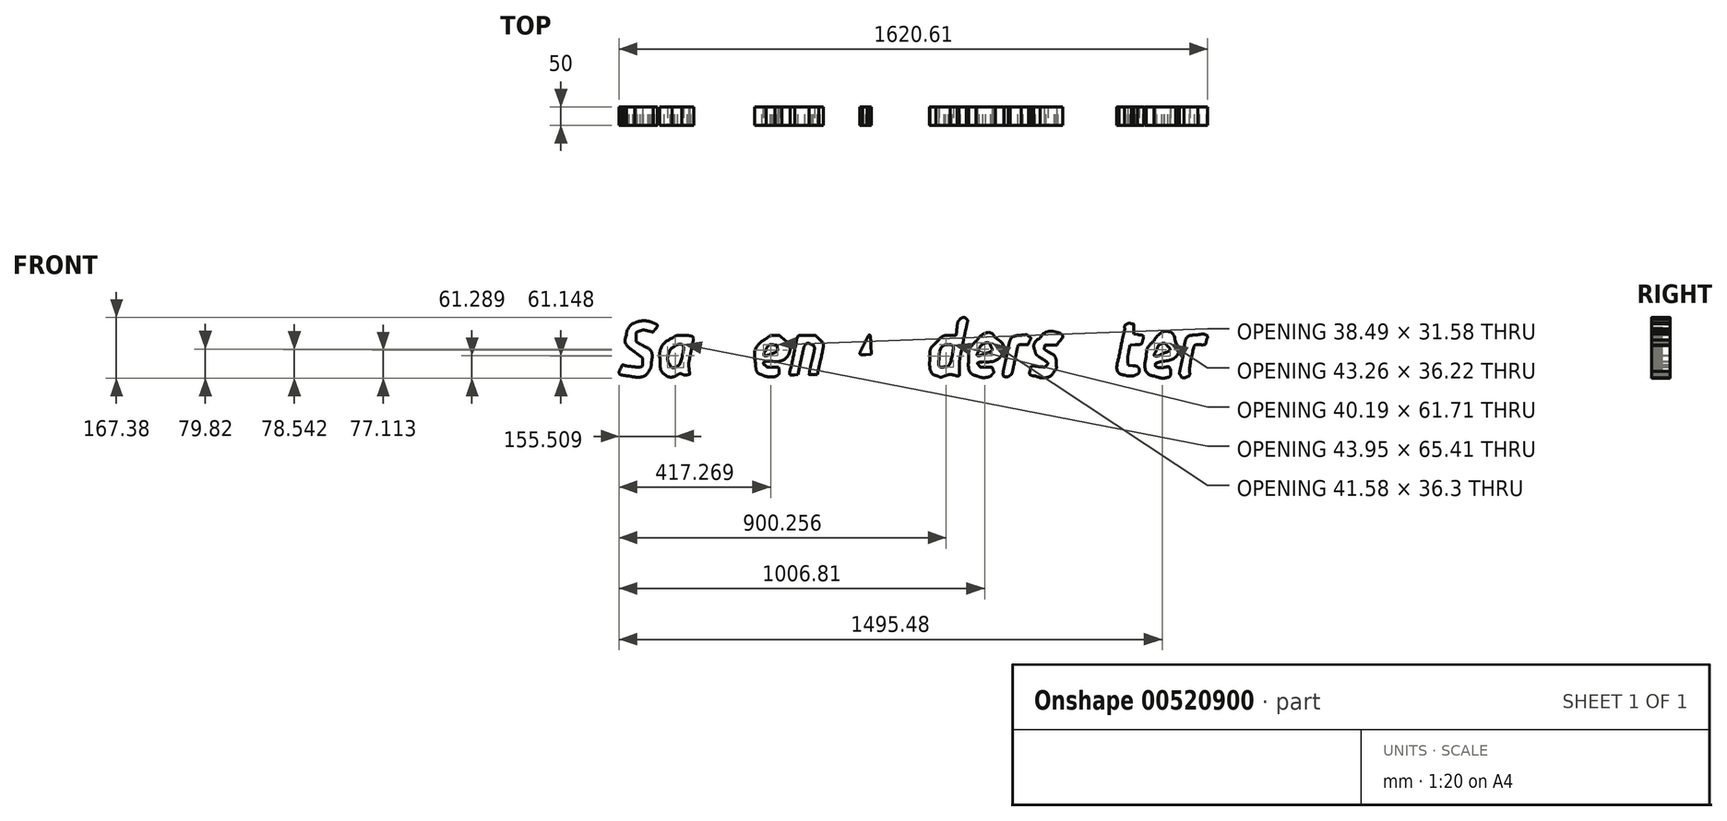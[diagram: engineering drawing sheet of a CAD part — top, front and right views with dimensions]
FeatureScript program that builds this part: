
annotation { "Feature Type Name" : "Feature", "Feature Type Description" : "" }
export const myFeature = defineFeature(function(context is Context, id is Id, definition is map)
    precondition{}
    {
        {
            var Q0;
            Q0=qCreatedBy(makeId("Front.planeOp"),FACE);
            var sketch = newSketch(context, id + "F0", { "sketchPlane" : qUnion([Q0])});
            skFitSpline(sketch, "E0", {"points": [v(-832.4, -78.37) * mm, v(-856.57, -74.84) * mm, v(-860.83, -70.17) * mm, v(-854.65, -53.92) * mm]});
            skFitSpline(sketch, "E1", {"points": [v(-854.65, -53.92) * mm, v(-852.6, -48.55) * mm, v(-851.2, -47.87) * mm, v(-845.3, -49.44) * mm]});
            skFitSpline(sketch, "E2", {"points": [v(-845.3, -49.44) * mm, v(-841.47, -50.45) * mm, v(-831.1, -51.83) * mm, v(-822.26, -52.5) * mm]});
            skFitSpline(sketch, "E3", {"points": [v(-822.26, -52.5) * mm, v(-803.08, -53.94) * mm, v(-796.37, -49.8) * mm, v(-796.37, -36.54) * mm]});
            skFitSpline(sketch, "E4", {"points": [v(-796.37, -36.54) * mm, v(-796.37, -29.53) * mm, v(-798.43, -26.67) * mm, v(-809.72, -18.05) * mm]});
            skFitSpline(sketch, "E5", {"points": [v(-809.72, -18.05) * mm, v(-836.26, 2.22) * mm, v(-844.67, 16.23) * mm, v(-841.08, 34.18) * mm]});
            skFitSpline(sketch, "E6", {"points": [v(-841.08, 34.18) * mm, v(-838.41, 47.53) * mm, v(-827.05, 63.97) * mm, v(-817.83, 67.82) * mm]});
            skFitSpline(sketch, "E7", {"points": [v(-817.83, 67.82) * mm, v(-806.68, 72.48) * mm, v(-778.28, 72.42) * mm, v(-767.03, 67.72) * mm]});
            skFitSpline(sketch, "E8", {"points": [v(-767.03, 67.72) * mm, v(-757.03, 63.54) * mm, v(-755.86, 58.07) * mm, v(-762.98, 48.8) * mm]});
            skFitSpline(sketch, "E9", {"points": [v(-762.98, 48.8) * mm, v(-767.45, 42.99) * mm, v(-768.18, 42.87) * mm, v(-780.63, 45.86) * mm]});
            skFitSpline(sketch, "E10", {"points": [v(-780.63, 45.86) * mm, v(-790.5, 48.22) * mm, v(-795.74, 48.27) * mm, v(-802.4, 46.07) * mm]});
            skFitSpline(sketch, "E11", {"points": [v(-802.4, 46.07) * mm, v(-812.07, 42.88) * mm, v(-814.18, 39.48) * mm, v(-814.18, 27.07) * mm]});
            skFitSpline(sketch, "E12", {"points": [v(-814.18, 27.07) * mm, v(-814.18, 17.85) * mm, v(-811.14, 14.56) * mm, v(-793.18, 4.3) * mm]});
            skFitSpline(sketch, "E13", {"points": [v(-793.18, 4.3) * mm, v(-776.34, -5.3) * mm, v(-769.88, -18.35) * mm, v(-771.56, -39.36) * mm]});
            skFitSpline(sketch, "E14", {"points": [v(-771.56, -39.36) * mm, v(-772.26, -48.1) * mm, v(-774.81, -58.03) * mm, v(-777.34, -61.88) * mm]});
            skFitSpline(sketch, "E15", {"points": [v(-777.34, -61.88) * mm, v(-786.08, -75.22) * mm, v(-808.33, -81.88) * mm, v(-832.4, -78.37) * mm]});
            skFitSpline(sketch, "E16", {"points": [v(13.27, -77.43) * mm, v(1.65, -72.38) * mm, v(-5.13, -55.86) * mm, v(-5.13, -32.6) * mm]});
            skFitSpline(sketch, "E17", {"points": [v(-5.13, -32.6) * mm, v(-5.13, -11.48) * mm, v(-0.66, 0.47) * mm, v(12.17, 13.69) * mm]});
            skFitSpline(sketch, "E18", {"points": [v(12.17, 13.69) * mm, v(26.49, 28.44) * mm, v(36.2, 33.5) * mm, v(50.88, 33.83) * mm]});
            skFitSpline(sketch, "E19", {"points": [v(50.88, 33.83) * mm, v(65.98, 34.17) * mm, v(67.23, 35.7) * mm, v(69.79, 56.78) * mm]});
            skFitSpline(sketch, "E20", {"points": [v(69.79, 56.78) * mm, v(70.76, 64.83) * mm, v(73.28, 73.13) * mm, v(75.37, 75.22) * mm]});
            skFitSpline(sketch, "E21", {"points": [v(75.37, 75.22) * mm, v(81.33, 81.18) * mm, v(91.43, 82.8) * mm, v(95.74, 78.49) * mm]});
            skFitSpline(sketch, "E22", {"points": [v(95.74, 78.49) * mm, v(99.06, 75.17) * mm, v(99.03, 72.66) * mm, v(95.5, 57.17) * mm]});
            skFitSpline(sketch, "E23", {"points": [v(95.5, 57.17) * mm, v(93.29, 47.5) * mm, v(89.09, 27.59) * mm, v(86.16, 12.9) * mm]});
            skFitSpline(sketch, "E24", {"points": [v(86.16, 12.9) * mm, v(83.24, -1.8) * mm, v(79.87, -18.4) * mm, v(78.67, -24) * mm]});
            skFitSpline(sketch, "E25", {"points": [v(78.67, -24) * mm, v(77.48, -29.6) * mm, v(76.46, -42.97) * mm, v(76.4, -53.72) * mm]});
            skFitSpline(sketch, "E26", {"points": [v(76.4, -53.72) * mm, v(76.27, -75.6) * mm, v(73.96, -78.2) * mm, v(57.4, -75.09) * mm]});
            skFitSpline(sketch, "E27", {"points": [v(57.4, -75.09) * mm, v(52.56, -74.18) * mm, v(44.62, -75.13) * mm, v(38.22, -77.39) * mm]});
            skFitSpline(sketch, "E28", {"points": [v(38.22, -77.39) * mm, v(25.08, -82.03) * mm, v(23.86, -82.03) * mm, v(13.27, -77.43) * mm]});
            skFitSpline(sketch, "E29", {"points": [v(45.61, -49.61) * mm, v(50.04, -44.27) * mm, v(59.23, 2.98) * mm, v(56.38, 5.82) * mm]});
            skFitSpline(sketch, "E30", {"points": [v(56.38, 5.82) * mm, v(55.1, 7.12) * mm, v(50.28, 7.8) * mm, v(45.7, 7.35) * mm]});
            skFitSpline(sketch, "E31", {"points": [v(45.7, 7.35) * mm, v(32.67, 6.07) * mm, v(22.2, -8.6) * mm, v(20.83, -27.5) * mm]});
            skFitSpline(sketch, "E32", {"points": [v(20.83, -27.5) * mm, v(19.44, -46.7) * mm, v(22.82, -53.26) * mm, v(34.08, -53.26) * mm]});
            skFitSpline(sketch, "E33", {"points": [v(34.08, -53.26) * mm, v(38.76, -53.26) * mm, v(43.95, -51.62) * mm, v(45.61, -49.61) * mm]});
            skFitSpline(sketch, "E34", {"points": [v(125.9, -78.32) * mm, v(108.94, -72.06) * mm, v(101.73, -58.36) * mm, v(101.73, -32.42) * mm]});
            skFitSpline(sketch, "E35", {"points": [v(101.73, -32.42) * mm, v(101.73, -12.23) * mm, v(107.6, 2.14) * mm, v(121.97, 17.13) * mm]});
            skFitSpline(sketch, "E36", {"points": [v(121.97, 17.13) * mm, v(140.93, 36.9) * mm, v(162.21, 41.06) * mm, v(174.93, 27.48) * mm]});
            skFitSpline(sketch, "E37", {"points": [v(174.93, 27.48) * mm, v(198.93, 1.86) * mm, v(180.94, -33.1) * mm, v(140.47, -39.49) * mm]});
            skFitSpline(sketch, "E38", {"points": [v(140.47, -39.49) * mm, v(127.69, -41.5) * mm, v(126.1, -43.2) * mm, v(130.86, -49.7) * mm]});
            skFitSpline(sketch, "E39", {"points": [v(130.86, -49.7) * mm, v(133.68, -53.56) * mm, v(137.62, -54.53) * mm, v(150.43, -54.53) * mm]});
            skFitSpline(sketch, "E40", {"points": [v(150.43, -54.53) * mm, v(165.66, -54.53) * mm, v(166.59, -54.88) * mm, v(168.95, -61.58) * mm]});
            skFitSpline(sketch, "E41", {"points": [v(168.95, -61.58) * mm, v(171, -67.37) * mm, v(170.51, -69.56) * mm, v(166.27, -73.8) * mm]});
            skFitSpline(sketch, "E42", {"points": [v(166.27, -73.8) * mm, v(160.04, -80.03) * mm, v(137.38, -82.56) * mm, v(125.9, -78.32) * mm]});
            skFitSpline(sketch, "E43", {"points": [v(148.39, -16.11) * mm, v(162.02, -11.46) * mm, v(166.94, -5.04) * mm, v(162.79, 2.72) * mm]});
            skFitSpline(sketch, "E44", {"points": [v(162.79, 2.72) * mm, v(157.07, 13.4) * mm, v(135.12, 5.48) * mm, v(129.5, -9.28) * mm]});
            skFitSpline(sketch, "E45", {"points": [v(129.5, -9.28) * mm, v(125.08, -20.9) * mm, v(129.56, -22.52) * mm, v(148.39, -16.11) * mm]});
            skFitSpline(sketch, "E46", {"points": [v(285.26, -78.7) * mm, v(272.13, -75.6) * mm, v(269.24, -71.47) * mm, v(272.34, -60.25) * mm]});
            skFitSpline(sketch, "E47", {"points": [v(293.34, -52.35) * mm, v(307.97, -53.59) * mm, v(312.38, -53.12) * mm, v(314.9, -50.09) * mm]});
            skFitSpline(sketch, "E48", {"points": [v(314.9, -50.09) * mm, v(319.65, -44.36) * mm, v(316.58, -39.62) * mm, v(301.31, -29.1) * mm]});
            skFitSpline(sketch, "E49", {"points": [v(301.31, -29.1) * mm, v(290.26, -21.5) * mm, v(286.93, -17.53) * mm, v(284.72, -9.33) * mm]});
            skFitSpline(sketch, "E50", {"points": [v(284.72, -9.33) * mm, v(281.07, 4.25) * mm, v(285.57, 16.14) * mm, v(298.24, 26.4) * mm]});
            skFitSpline(sketch, "E51", {"points": [v(298.24, 26.4) * mm, v(320.16, 44.13) * mm, v(359.88, 33.93) * mm, v(348.4, 13.5) * mm]});
            skFitSpline(sketch, "E52", {"points": [v(348.4, 13.5) * mm, v(344.77, 7.03) * mm, v(343.32, 6.53) * mm, v(328.05, 6.53) * mm]});
            skFitSpline(sketch, "E53", {"points": [v(328.05, 6.53) * mm, v(313.06, 6.53) * mm, v(311.55, 6.04) * mm, v(310.82, 0.94) * mm]});
            skFitSpline(sketch, "E54", {"points": [v(310.82, 0.94) * mm, v(310.24, -3.2) * mm, v(312.55, -6.26) * mm, v(319.73, -10.84) * mm]});
            skFitSpline(sketch, "E55", {"points": [v(319.73, -10.84) * mm, v(336.4, -21.47) * mm, v(341.61, -28.9) * mm, v(342.82, -43.7) * mm]});
            skFitSpline(sketch, "E56", {"points": [v(342.82, -43.7) * mm, v(343.73, -54.78) * mm, v(342.93, -58.33) * mm, v(338.15, -64.39) * mm]});
            skFitSpline(sketch, "E57", {"points": [v(338.15, -64.39) * mm, v(327.14, -78.34) * mm, v(306.9, -83.81) * mm, v(285.26, -78.7) * mm]});
            skLineSegment(sketch, "E58", {"start": v(272.34, -60.25) * mm, "end": v(274.95, -50.8) * mm});
            skLineSegment(sketch, "E59", {"start": v(274.95, -50.8) * mm, "end": v(293.34, -52.35) * mm});
            skFitSpline(sketch, "E60", {"points": [v(416.9, -77.4) * mm, v(400.2, -72.07) * mm, v(397.47, -68.03) * mm, v(402.89, -56.67) * mm]});
            skFitSpline(sketch, "E61", {"points": [v(402.89, -56.67) * mm, v(406.73, -48.61) * mm, v(407.97, -47.81) * mm, v(414.11, -49.45) * mm]});
            skFitSpline(sketch, "E62", {"points": [v(414.11, -49.45) * mm, v(417.91, -50.46) * mm, v(428.02, -51.82) * mm, v(436.58, -52.47) * mm]});
            skFitSpline(sketch, "E63", {"points": [v(436.58, -52.47) * mm, v(451.13, -53.58) * mm, v(452.48, -53.21) * mm, v(457.57, -46.75) * mm]});
            skFitSpline(sketch, "E64", {"points": [v(457.57, -46.75) * mm, v(466.75, -35.08) * mm, v(466.96, -35.45) * mm, v(431.27, -2.8) * mm]});
            skFitSpline(sketch, "E65", {"points": [v(431.27, -2.8) * mm, v(415.1, 12) * mm, v(412.84, 28.92) * mm, v(424.26, 49.67) * mm]});
            skFitSpline(sketch, "E66", {"points": [v(424.26, 49.67) * mm, v(433.77, 66.95) * mm, v(443.58, 72.21) * mm, v(466.48, 72.32) * mm]});
            skFitSpline(sketch, "E67", {"points": [v(466.48, 72.32) * mm, v(495, 72.44) * mm, v(506.72, 63.65) * mm, v(498.5, 48.3) * mm]});
            skFitSpline(sketch, "E68", {"points": [v(498.5, 48.3) * mm, v(496.08, 43.78) * mm, v(494.02, 43.47) * mm, v(475.94, 44.98) * mm]});
            skFitSpline(sketch, "E69", {"points": [v(475.94, 44.98) * mm, v(457.8, 46.5) * mm, v(455.56, 46.16) * mm, v(450.61, 41.22) * mm]});
            skFitSpline(sketch, "E70", {"points": [v(450.61, 41.22) * mm, v(438.92, 29.53) * mm, v(444.77, 18.04) * mm, v(470.63, 1.88) * mm]});
            skFitSpline(sketch, "E71", {"points": [v(470.63, 1.88) * mm, v(480.9, -4.54) * mm, v(490.98, -22.57) * mm, v(490.98, -34.5) * mm]});
            skFitSpline(sketch, "E72", {"points": [v(490.98, -34.5) * mm, v(490.98, -44.42) * mm, v(483.22, -63.14) * mm, v(476.68, -68.98) * mm]});
            skFitSpline(sketch, "E73", {"points": [v(476.68, -68.98) * mm, v(465.2, -79.23) * mm, v(435.67, -83.4) * mm, v(416.9, -77.4) * mm]});
            skFitSpline(sketch, "E74", {"points": [v(614.68, -78.6) * mm, v(596.44, -73.15) * mm, v(587.03, -53.04) * mm, v(590.24, -26.35) * mm]});
            skFitSpline(sketch, "E75", {"points": [v(590.24, -26.35) * mm, v(592.6, -6.7) * mm, v(597.58, 3.7) * mm, v(611.7, 18.43) * mm]});
            skFitSpline(sketch, "E76", {"points": [v(611.7, 18.43) * mm, v(634.54, 42.27) * mm, v(661.63, 40.55) * mm, v(671.45, 14.64) * mm]});
            skFitSpline(sketch, "E77", {"points": [v(671.45, 14.64) * mm, v(680.86, -10.2) * mm, v(666.7, -29.94) * mm, v(633.46, -38.3) * mm]});
            skFitSpline(sketch, "E78", {"points": [v(633.46, -38.3) * mm, v(623.4, -40.84) * mm, v(616.92, -43.81) * mm, v(616.92, -45.88) * mm]});
            skFitSpline(sketch, "E79", {"points": [v(616.92, -45.88) * mm, v(616.92, -51.83) * mm, v(628.77, -55.84) * mm, v(641.48, -54.2) * mm]});
            skFitSpline(sketch, "E80", {"points": [v(641.48, -54.2) * mm, v(651.92, -52.85) * mm, v(653.67, -53.33) * mm, v(656.32, -58.29) * mm]});
            skFitSpline(sketch, "E81", {"points": [v(656.32, -58.29) * mm, v(657.98, -61.38) * mm, v(658.65, -66.61) * mm, v(657.82, -69.92) * mm]});
            skFitSpline(sketch, "E82", {"points": [v(657.82, -69.92) * mm, v(655.43, -79.46) * mm, v(632.77, -84.03) * mm, v(614.68, -78.6) * mm]});
            skFitSpline(sketch, "E83", {"points": [v(639.66, -15.16) * mm, v(653.29, -9.32) * mm, v(656.23, -4.17) * mm, v(649.9, 2.81) * mm]});
            skFitSpline(sketch, "E84", {"points": [v(649.9, 2.81) * mm, v(641.53, 12.07) * mm, v(626.43, 7.35) * mm, v(619.78, -6.61) * mm]});
            skFitSpline(sketch, "E85", {"points": [v(619.78, -6.61) * mm, v(612.8, -21.25) * mm, v(619.11, -23.97) * mm, v(639.66, -15.16) * mm]});
            skFitSpline(sketch, "E86", {"points": [v(-735.87, -72.96) * mm, v(-743.4, -66.75) * mm, v(-747.86, -52.1) * mm, v(-747.96, -33.2) * mm]});
            skFitSpline(sketch, "E87", {"points": [v(-747.96, -33.2) * mm, v(-748.1, -8.56) * mm, v(-736.42, 12.55) * mm, v(-715.2, 26) * mm]});
            skFitSpline(sketch, "E88", {"points": [v(-715.2, 26) * mm, v(-705.73, 32) * mm, v(-701.01, 33.25) * mm, v(-687.61, 33.25) * mm]});
            skFitSpline(sketch, "E89", {"points": [v(-687.61, 33.25) * mm, v(-671.7, 33.25) * mm, v(-656.44, 28.2) * mm, v(-656.44, 22.93) * mm]});
            skFitSpline(sketch, "E90", {"points": [v(-656.44, 22.93) * mm, v(-656.44, 21.53) * mm, v(-659.4, 5.82) * mm, v(-663.02, -11.99) * mm]});
            skFitSpline(sketch, "E91", {"points": [v(-663.02, -11.99) * mm, v(-667.89, -35.9) * mm, v(-669.19, -48.15) * mm, v(-668, -58.9) * mm]});
            skFitSpline(sketch, "E92", {"points": [v(-668, -58.9) * mm, v(-666.42, -73.04) * mm, v(-666.57, -73.5) * mm, v(-673.04, -75.13) * mm]});
            skFitSpline(sketch, "E93", {"points": [v(-673.04, -75.13) * mm, v(-676.71, -76.05) * mm, v(-682.54, -75.5) * mm, v(-686, -73.93) * mm]});
            skFitSpline(sketch, "E94", {"points": [v(-686, -73.93) * mm, v(-690.95, -71.68) * mm, v(-693.9, -71.88) * mm, v(-699.68, -74.88) * mm]});
            skFitSpline(sketch, "E95", {"points": [v(-699.68, -74.88) * mm, v(-710.86, -80.66) * mm, v(-727.61, -79.77) * mm, v(-735.87, -72.96) * mm]});
            skFitSpline(sketch, "E96", {"points": [v(-699.02, -50.08) * mm, v(-694.76, -46.83) * mm, v(-683.42, 1.57) * mm, v(-685.96, 5.69) * mm]});
            skFitSpline(sketch, "E97", {"points": [v(-685.96, 5.69) * mm, v(-688.13, 9.2) * mm, v(-700.72, 8.07) * mm, v(-706.79, 3.82) * mm]});
            skFitSpline(sketch, "E98", {"points": [v(-706.79, 3.82) * mm, v(-719.65, -5.19) * mm, v(-727.15, -34.9) * mm, v(-719.95, -48.33) * mm]});
            skFitSpline(sketch, "E99", {"points": [v(-719.95, -48.33) * mm, v(-716.92, -54) * mm, v(-705.45, -54.96) * mm, v(-699.02, -50.08) * mm]});
            skFitSpline(sketch, "E100", {"points": [v(-467.34, -74.99) * mm, v(-478.7, -70.04) * mm, v(-483.32, -61.6) * mm, v(-485.1, -42.54) * mm]});
            skFitSpline(sketch, "E101", {"points": [v(-485.1, -42.54) * mm, v(-487.7, -14.63) * mm, v(-478.08, 7.64) * mm, v(-456.16, 24.38) * mm]});
            skFitSpline(sketch, "E102", {"points": [v(-456.16, 24.38) * mm, v(-446.34, 31.87) * mm, v(-442.5, 33.25) * mm, v(-431.36, 33.25) * mm]});
            skFitSpline(sketch, "E103", {"points": [v(-431.36, 33.25) * mm, v(-420.87, 33.25) * mm, v(-417.14, 32.07) * mm, v(-413.13, 27.52) * mm]});
            skFitSpline(sketch, "E104", {"points": [v(-413.13, 27.52) * mm, v(-389.9, 1.19) * mm, v(-406.36, -33.37) * mm, v(-443.95, -37.25) * mm]});
            skFitSpline(sketch, "E105", {"points": [v(-443.95, -37.25) * mm, v(-459.68, -38.88) * mm, v(-464.06, -43.19) * mm, v(-457.09, -50.16) * mm]});
            skFitSpline(sketch, "E106", {"points": [v(-457.09, -50.16) * mm, v(-454.17, -53.08) * mm, v(-448.23, -54.34) * mm, v(-437.02, -54.42) * mm]});
            skFitSpline(sketch, "E107", {"points": [v(-420.26, -63.32) * mm, v(-419.68, -69.5) * mm, v(-420.77, -73.1) * mm, v(-423.93, -75.4) * mm]});
            skFitSpline(sketch, "E108", {"points": [v(-423.93, -75.4) * mm, v(-429.86, -79.74) * mm, v(-457.02, -79.47) * mm, v(-467.34, -74.99) * mm]});
            skLineSegment(sketch, "E109", {"start": v(-437.02, -54.42) * mm, "end": v(-421.1, -54.53) * mm});
            skLineSegment(sketch, "E110", {"start": v(-421.1, -54.53) * mm, "end": v(-420.26, -63.32) * mm});
            skFitSpline(sketch, "E111", {"points": [v(-442.47, -17.28) * mm, v(-430.03, -13.1) * mm, v(-424.55, -7.53) * mm, v(-425.43, 0.04) * mm]});
            skFitSpline(sketch, "E112", {"points": [v(-425.43, 0.04) * mm, v(-426.02, 5.1) * mm, v(-427.82, 6.72) * mm, v(-433.6, 7.38) * mm]});
            skFitSpline(sketch, "E113", {"points": [v(-433.6, 7.38) * mm, v(-443.8, 8.54) * mm, v(-451.41, 3.87) * mm, v(-456.4, -6.6) * mm]});
            skFitSpline(sketch, "E114", {"points": [v(-456.4, -6.6) * mm, v(-462.82, -20.05) * mm, v(-459.13, -22.87) * mm, v(-442.47, -17.28) * mm]});
            skFitSpline(sketch, "E115", {"points": [v(-249.22, -76.3) * mm, v(-252.22, -74.4) * mm, v(-248.62, -65.43) * mm, v(-229.57, -27.36) * mm]});
            skFitSpline(sketch, "E116", {"points": [v(-229.57, -27.36) * mm, v(-205.24, 21.28) * mm, v(-184.06, 59.36) * mm, v(-177.11, 66.96) * mm]});
            skFitSpline(sketch, "E117", {"points": [v(-177.11, 66.96) * mm, v(-172.39, 72.13) * mm, v(-157.07, 72.95) * mm, v(-153.37, 68.23) * mm]});
            skFitSpline(sketch, "E118", {"points": [v(-153.37, 68.23) * mm, v(-150.18, 64.16) * mm, v(-146.46, 39.3) * mm, v(-139.84, -22.27) * mm]});
            skFitSpline(sketch, "E119", {"points": [v(-139.84, -22.27) * mm, v(-134.1, -75.62) * mm, v(-134.51, -78.73) * mm, v(-147.28, -78.66) * mm]});
            skFitSpline(sketch, "E120", {"points": [v(-147.28, -78.66) * mm, v(-158.15, -78.6) * mm, v(-161.33, -74.85) * mm, v(-162.78, -60.4) * mm]});
            skFitSpline(sketch, "E121", {"points": [v(-188.96, -46.17) * mm, v(-216.5, -45.36) * mm, v(-213.34, -43.52) * mm, v(-221.32, -65.01) * mm]});
            skFitSpline(sketch, "E122", {"points": [v(-221.32, -65.01) * mm, v(-225.5, -76.26) * mm, v(-240.01, -82.13) * mm, v(-249.22, -76.3) * mm]});
            skLineSegment(sketch, "E123", {"start": v(-162.78, -60.4) * mm, "end": v(-164.14, -46.9) * mm});
            skLineSegment(sketch, "E124", {"start": v(-164.14, -46.9) * mm, "end": v(-188.96, -46.17) * mm});
            skFitSpline(sketch, "E125", {"points": [v(-167.57, 6.53) * mm, v(-168.06, 20.53) * mm, v(-169.4, 32.97) * mm, v(-170.54, 34.19) * mm]});
            skFitSpline(sketch, "E126", {"points": [v(-170.54, 34.19) * mm, v(-171.7, 35.4) * mm, v(-174.85, 31.97) * mm, v(-177.56, 26.55) * mm]});
            skFitSpline(sketch, "E127", {"points": [v(-177.56, 26.55) * mm, v(-180.28, 21.14) * mm, v(-186.14, 9.52) * mm, v(-190.6, 0.74) * mm]});
            skFitSpline(sketch, "E128", {"points": [v(-190.6, 0.74) * mm, v(-195.05, -8.05) * mm, v(-197.98, -16.4) * mm, v(-197.1, -17.83) * mm]});
            skFitSpline(sketch, "E129", {"points": [v(-197.1, -17.83) * mm, v(-196.21, -19.26) * mm, v(-189.01, -20.08) * mm, v(-181.09, -19.67) * mm]});
            skFitSpline(sketch, "E130", {"points": [v(-113.55, -75.03) * mm, v(-115.05, -71.12) * mm, v(-104.47, -16.2) * mm, v(-97.4, 8.79) * mm]});
            skFitSpline(sketch, "E131", {"points": [v(-97.4, 8.79) * mm, v(-92.42, 26.38) * mm, v(-85.25, 32.09) * mm, v(-64.93, 34.63) * mm]});
            skFitSpline(sketch, "E132", {"points": [v(-64.93, 34.63) * mm, v(-39.6, 37.8) * mm, v(-22.92, 22.87) * mm, v(-22.95, -2.9) * mm]});
            skFitSpline(sketch, "E133", {"points": [v(-22.95, -2.9) * mm, v(-22.97, -16.06) * mm, v(-34.26, -70.68) * mm, v(-37.66, -74.08) * mm]});
            skFitSpline(sketch, "E134", {"points": [v(-37.66, -74.08) * mm, v(-38.99, -75.41) * mm, v(-44.52, -76.14) * mm, v(-49.95, -75.7) * mm]});
            skFitSpline(sketch, "E135", {"points": [v(-49.95, -75.7) * mm, v(-61.62, -74.73) * mm, v(-61.42, -77.03) * mm, v(-53.6, -33.73) * mm]});
            skFitSpline(sketch, "E136", {"points": [v(-53.6, -33.73) * mm, v(-46.92, 3.18) * mm, v(-48.16, 8.57) * mm, v(-63, 7.31) * mm]});
            skLineSegment(sketch, "E137", {"start": v(-181.09, -19.67) * mm, "end": v(-166.68, -18.9) * mm});
            skLineSegment(sketch, "E138", {"start": v(-166.68, -18.9) * mm, "end": v(-167.57, 6.53) * mm});
            skFitSpline(sketch, "E139", {"points": [v(-78.09, -18.9) * mm, v(-81.33, -32.9) * mm, v(-85.12, -50.65) * mm, v(-86.5, -58.34) * mm]});
            skFitSpline(sketch, "E140", {"points": [v(-86.5, -58.34) * mm, v(-87.91, -66.18) * mm, v(-90.93, -73.74) * mm, v(-93.36, -75.52) * mm]});
            skFitSpline(sketch, "E141", {"points": [v(-93.36, -75.52) * mm, v(-99.25, -79.84) * mm, v(-111.82, -79.54) * mm, v(-113.55, -75.03) * mm]});
            skLineSegment(sketch, "E142", {"start": v(-63, 7.31) * mm, "end": v(-72.18, 6.53) * mm});
            skLineSegment(sketch, "E143", {"start": v(-72.18, 6.53) * mm, "end": v(-78.09, -18.9) * mm});
            skFitSpline(sketch, "E144", {"points": [v(196.95, -75.31) * mm, v(196.23, -73.45) * mm, v(198.65, -57.7) * mm, v(202.32, -40.33) * mm]});
            skFitSpline(sketch, "E145", {"points": [v(202.32, -40.33) * mm, v(205.99, -22.95) * mm, v(210.14, -3.03) * mm, v(211.55, 3.93) * mm]});
            skFitSpline(sketch, "E146", {"points": [v(211.55, 3.93) * mm, v(212.96, 10.9) * mm, v(215.19, 18.61) * mm, v(216.5, 21.08) * mm]});
            skFitSpline(sketch, "E147", {"points": [v(216.5, 21.08) * mm, v(220.05, 27.7) * mm, v(230.9, 32.33) * mm, v(247.1, 34.16) * mm]});
            skFitSpline(sketch, "E148", {"points": [v(247.1, 34.16) * mm, v(258.99, 35.5) * mm, v(262.5, 34.94) * mm, v(267.42, 30.95) * mm]});
            skFitSpline(sketch, "E149", {"points": [v(267.42, 30.95) * mm, v(273.28, 26.2) * mm, v(273.3, 25.99) * mm, v(269, 16.97) * mm]});
            skFitSpline(sketch, "E150", {"points": [v(269, 16.97) * mm, v(264.84, 8.23) * mm, v(264.03, 7.8) * mm, v(251.8, 7.8) * mm]});
            skFitSpline(sketch, "E151", {"points": [v(251.8, 7.8) * mm, v(243.86, 7.8) * mm, v(238.49, 6.59) * mm, v(237.73, 4.62) * mm]});
            skFitSpline(sketch, "E152", {"points": [v(237.73, 4.62) * mm, v(237.07, 2.87) * mm, v(233.1, -15.16) * mm, v(228.94, -35.45) * mm]});
            skFitSpline(sketch, "E153", {"points": [v(228.94, -35.45) * mm, v(223.76, -60.66) * mm, v(219.99, -73.34) * mm, v(217.03, -75.52) * mm]});
            skFitSpline(sketch, "E154", {"points": [v(217.03, -75.52) * mm, v(211.3, -79.72) * mm, v(198.59, -79.59) * mm, v(196.95, -75.31) * mm]});
            skFitSpline(sketch, "E155", {"points": [v(532.76, -76.02) * mm, v(515.39, -70.85) * mm, v(509.91, -55.44) * mm, v(515.39, -27.1) * mm]});
            skFitSpline(sketch, "E156", {"points": [v(515.39, -27.1) * mm, v(524.65, 20.8) * mm, v(527.09, 32.54) * mm, v(529.3, 39.79) * mm]});
            skFitSpline(sketch, "E157", {"points": [v(529.3, 39.79) * mm, v(530.62, 44.08) * mm, v(531.7, 50.07) * mm, v(531.7, 53.09) * mm]});
            skFitSpline(sketch, "E158", {"points": [v(531.7, 53.09) * mm, v(531.7, 59.8) * mm, v(542, 67.01) * mm, v(549.99, 65.88) * mm]});
            skFitSpline(sketch, "E159", {"points": [v(549.99, 65.88) * mm, v(555.3, 65.13) * mm, v(555.86, 63.73) * mm, v(555.86, 51.06) * mm]});
            skFitSpline(sketch, "E160", {"points": [v(566.72, 35.61) * mm, v(579.84, 33.86) * mm, v(583.73, 30.47) * mm, v(581.65, 22.62) * mm]});
            skFitSpline(sketch, "E161", {"points": [v(581.65, 22.62) * mm, v(578.66, 11.4) * mm, v(575.51, 9.19) * mm, v(560.57, 7.84) * mm]});
            skLineSegment(sketch, "E162", {"start": v(555.86, 51.06) * mm, "end": v(555.86, 37.07) * mm});
            skLineSegment(sketch, "E163", {"start": v(555.86, 37.07) * mm, "end": v(566.72, 35.61) * mm});
            skFitSpline(sketch, "E164", {"points": [v(542.6, -11.28) * mm, v(540.76, -21.07) * mm, v(539.55, -33.67) * mm, v(539.92, -39.26) * mm]});
            skLineSegment(sketch, "E165", {"start": v(560.57, 7.84) * mm, "end": v(545.96, 6.53) * mm});
            skLineSegment(sketch, "E166", {"start": v(545.96, 6.53) * mm, "end": v(542.6, -11.28) * mm});
            skFitSpline(sketch, "E167", {"points": [v(553.27, -50.24) * mm, v(560.24, -50.68) * mm, v(566.8, -52.4) * mm, v(567.86, -54.06) * mm]});
            skFitSpline(sketch, "E168", {"points": [v(567.86, -54.06) * mm, v(571.4, -59.63) * mm, v(569.97, -70.83) * mm, v(565.4, -73.22) * mm]});
            skFitSpline(sketch, "E169", {"points": [v(565.4, -73.22) * mm, v(558.1, -77.06) * mm, v(541.14, -78.51) * mm, v(532.76, -76.02) * mm]});
            skLineSegment(sketch, "E170", {"start": v(539.92, -39.26) * mm, "end": v(540.6, -49.44) * mm});
            skLineSegment(sketch, "E171", {"start": v(540.6, -49.44) * mm, "end": v(553.27, -50.24) * mm});
            skFitSpline(sketch, "E172", {"points": [v(684.64, -75.24) * mm, v(682.48, -72.63) * mm, v(683.1, -65.55) * mm, v(687.16, -46.62) * mm]});
            skFitSpline(sketch, "E173", {"points": [v(687.16, -46.62) * mm, v(690.13, -32.78) * mm, v(693.45, -15.73) * mm, v(694.54, -8.73) * mm]});
            skFitSpline(sketch, "E174", {"points": [v(694.54, -8.73) * mm, v(699.21, 21.33) * mm, v(708.61, 32.14) * mm, v(732.55, 34.98) * mm]});
            skFitSpline(sketch, "E175", {"points": [v(732.55, 34.98) * mm, v(749.35, 36.97) * mm, v(759.43, 31.16) * mm, v(756.87, 20.97) * mm]});
            skFitSpline(sketch, "E176", {"points": [v(756.87, 20.97) * mm, v(754.16, 10.19) * mm, v(750.68, 7.8) * mm, v(737.6, 7.8) * mm]});
            skFitSpline(sketch, "E177", {"points": [v(737.6, 7.8) * mm, v(730.86, 7.8) * mm, v(724.75, 6.83) * mm, v(724, 5.64) * mm]});
            skFitSpline(sketch, "E178", {"points": [v(724, 5.64) * mm, v(722.28, 2.84) * mm, v(709.78, -59.9) * mm, v(709.78, -65.79) * mm]});
            skFitSpline(sketch, "E179", {"points": [v(709.78, -65.79) * mm, v(709.78, -76.17) * mm, v(691.2, -83.15) * mm, v(684.64, -75.24) * mm]});
            skFitSpline(sketch, "E180", {"points": [v(762.39, -75.9) * mm, v(757.57, -73.04) * mm, v(757.77, -65.56) * mm, v(763.27, -43.08) * mm]});
            skFitSpline(sketch, "E181", {"points": [v(763.27, -43.08) * mm, v(764.47, -38.18) * mm, v(766.6, -29.02) * mm, v(768, -22.73) * mm]});
            skFitSpline(sketch, "E182", {"points": [v(768, -22.73) * mm, v(769.4, -16.43) * mm, v(772.26, -3.84) * mm, v(774.36, 5.26) * mm]});
            skFitSpline(sketch, "E183", {"points": [v(774.36, 5.26) * mm, v(776.45, 14.36) * mm, v(780.11, 32.67) * mm, v(782.48, 45.97) * mm]});
            skFitSpline(sketch, "E184", {"points": [v(782.48, 45.97) * mm, v(787.97, 76.73) * mm, v(787.5, 75.72) * mm, v(798.04, 79.2) * mm]});
            skFitSpline(sketch, "E185", {"points": [v(798.04, 79.2) * mm, v(805.21, 81.57) * mm, v(807.66, 81.47) * mm, v(810.38, 78.69) * mm]});
            skFitSpline(sketch, "E186", {"points": [v(810.38, 78.69) * mm, v(813.23, 75.8) * mm, v(812.94, 71.24) * mm, v(808.63, 51.06) * mm]});
            skFitSpline(sketch, "E187", {"points": [v(808.63, 51.06) * mm, v(800.83, 14.47) * mm, v(798.49, -0.34) * mm, v(800.22, -2.07) * mm]});
            skFitSpline(sketch, "E188", {"points": [v(800.22, -2.07) * mm, v(801.09, -2.93) * mm, v(810.24, 5.23) * mm, v(820.57, 16.08) * mm]});
            skFitSpline(sketch, "E189", {"points": [v(820.57, 16.08) * mm, v(838.6, 35) * mm, v(843.82, 37.9) * mm, v(853.32, 34.25) * mm]});
            skFitSpline(sketch, "E190", {"points": [v(853.32, 34.25) * mm, v(861.23, 31.21) * mm, v(857.17, 22.34) * mm, v(839.53, 4.16) * mm]});
            skFitSpline(sketch, "E191", {"points": [v(839.53, 4.16) * mm, v(829.33, -6.36) * mm, v(821.73, -16.42) * mm, v(821.73, -19.39) * mm]});
            skFitSpline(sketch, "E192", {"points": [v(821.73, -19.39) * mm, v(821.73, -22.23) * mm, v(826.3, -34.34) * mm, v(831.9, -46.28) * mm]});
            skFitSpline(sketch, "E193", {"points": [v(831.9, -46.28) * mm, v(837.5, -58.23) * mm, v(842.08, -69.22) * mm, v(842.08, -70.71) * mm]});
            skFitSpline(sketch, "E194", {"points": [v(842.08, -70.71) * mm, v(842.08, -74.25) * mm, v(833.67, -78.7) * mm, v(826.98, -78.7) * mm]});
            skFitSpline(sketch, "E195", {"points": [v(826.98, -78.7) * mm, v(819.7, -78.7) * mm, v(811.55, -69.84) * mm, v(811.55, -61.94) * mm]});
            skFitSpline(sketch, "E196", {"points": [v(811.55, -61.94) * mm, v(811.55, -54.5) * mm, v(796.75, -32.32) * mm, v(792.69, -33.68) * mm]});
            skFitSpline(sketch, "E197", {"points": [v(792.69, -33.68) * mm, v(791.22, -34.17) * mm, v(788.8, -42.79) * mm, v(787.28, -52.84) * mm]});
            skFitSpline(sketch, "E198", {"points": [v(787.28, -52.84) * mm, v(785.77, -62.9) * mm, v(783.45, -72.17) * mm, v(782.14, -73.45) * mm]});
            skFitSpline(sketch, "E199", {"points": [v(782.14, -73.45) * mm, v(778.05, -77.45) * mm, v(767.25, -78.8) * mm, v(762.39, -75.9) * mm]});
            skFitSpline(sketch, "E200", {"points": [v(-641.7, -74.78) * mm, v(-643.24, -73.24) * mm, v(-639.16, -51.2) * mm, v(-628.99, -6.19) * mm]});
            skFitSpline(sketch, "E201", {"points": [v(-628.99, -6.19) * mm, v(-622.25, 23.62) * mm, v(-621.88, 24.45) * mm, v(-613.19, 28.79) * mm]});
            skFitSpline(sketch, "E202", {"points": [v(-613.19, 28.79) * mm, v(-600.07, 35.34) * mm, v(-576.9, 34.78) * mm, v(-567.29, 27.68) * mm]});
            skFitSpline(sketch, "E203", {"points": [v(-552.23, 27.68) * mm, v(-546.88, 31.64) * mm, v(-541.07, 33.25) * mm, v(-532.14, 33.25) * mm]});
            skFitSpline(sketch, "E204", {"points": [v(-532.14, 33.25) * mm, v(-520.98, 33.25) * mm, v(-518.7, 32.26) * mm, v(-511.8, 24.4) * mm]});
            skFitSpline(sketch, "E205", {"points": [v(-511.8, 24.4) * mm, v(-499.37, 10.23) * mm, v(-498.81, 1.7) * mm, v(-507.46, -41.8) * mm]});
            skFitSpline(sketch, "E206", {"points": [v(-507.46, -41.8) * mm, v(-514.17, -75.58) * mm, v(-514.5, -76.15) * mm, v(-526.96, -76.15) * mm]});
            skLineSegment(sketch, "E207", {"start": v(-567.29, 27.68) * mm, "end": v(-559.76, 22.11) * mm});
            skLineSegment(sketch, "E208", {"start": v(-559.76, 22.11) * mm, "end": v(-552.23, 27.68) * mm});
            skFitSpline(sketch, "E209", {"points": [v(-536.09, -66.61) * mm, v(-535.3, -61.37) * mm, v(-532.88, -49.06) * mm, v(-530.71, -39.26) * mm]});
            skFitSpline(sketch, "E210", {"points": [v(-530.71, -39.26) * mm, v(-528.54, -29.47) * mm, v(-526.75, -15.42) * mm, v(-526.73, -8.04) * mm]});
            skFitSpline(sketch, "E211", {"points": [v(-526.73, -8.04) * mm, v(-526.69, 3.94) * mm, v(-527.39, 5.69) * mm, v(-533.28, 8.38) * mm]});
            skFitSpline(sketch, "E212", {"points": [v(-533.28, 8.38) * mm, v(-543.84, 13.19) * mm, v(-553.2, 6.61) * mm, v(-554.13, -6.27) * mm]});
            skFitSpline(sketch, "E213", {"points": [v(-554.13, -6.27) * mm, v(-554.74, -14.66) * mm, v(-560.67, -46.23) * mm, v(-566.18, -70.43) * mm]});
            skFitSpline(sketch, "E214", {"points": [v(-566.18, -70.43) * mm, v(-567.26, -75.17) * mm, v(-569.2, -76.15) * mm, v(-577.47, -76.15) * mm]});
            skFitSpline(sketch, "E215", {"points": [v(-577.47, -76.15) * mm, v(-582.95, -76.15) * mm, v(-587.97, -75.3) * mm, v(-588.61, -74.25) * mm]});
            skFitSpline(sketch, "E216", {"points": [v(-588.61, -74.25) * mm, v(-589.26, -73.2) * mm, v(-586.82, -56.07) * mm, v(-583.19, -36.19) * mm]});
            skFitSpline(sketch, "E217", {"points": [v(-583.19, -36.19) * mm, v(-576.76, -0.97) * mm, v(-576.7, 0.1) * mm, v(-581.29, 5.15) * mm]});
            skFitSpline(sketch, "E218", {"points": [v(-581.29, 5.15) * mm, v(-583.87, 8.01) * mm, v(-587.88, 10.35) * mm, v(-590.2, 10.35) * mm]});
            skFitSpline(sketch, "E219", {"points": [v(-590.2, 10.35) * mm, v(-600.38, 10.35) * mm, v(-603.51, 4) * mm, v(-610.93, -31.7) * mm]});
            skFitSpline(sketch, "E220", {"points": [v(-610.93, -31.7) * mm, v(-620.76, -79.05) * mm, v(-619.47, -76.15) * mm, v(-630.74, -76.15) * mm]});
            skFitSpline(sketch, "E221", {"points": [v(-630.74, -76.15) * mm, v(-636.01, -76.15) * mm, v(-640.94, -75.54) * mm, v(-641.7, -74.78) * mm]});
            skLineSegment(sketch, "E222", {"start": v(-526.96, -76.15) * mm, "end": v(-537.53, -76.15) * mm});
            skLineSegment(sketch, "E223", {"start": v(-537.53, -76.15) * mm, "end": v(-536.09, -66.61) * mm});
            skFitSpline(sketch, "E224", {"points": [v(-389.96, -74.38) * mm, v(-391.1, -72.34) * mm, v(-387.3, -52.2) * mm, v(-376.45, -2.72) * mm]});
            skFitSpline(sketch, "E225", {"points": [v(-376.45, -2.72) * mm, v(-369.37, 29.59) * mm, v(-365.43, 33.22) * mm, v(-337.53, 33.24) * mm]});
            skFitSpline(sketch, "E226", {"points": [v(-337.53, 33.24) * mm, v(-321.17, 33.25) * mm, v(-319.58, 32.72) * mm, v(-311.65, 24.8) * mm]});
            skFitSpline(sketch, "E227", {"points": [v(-311.65, 24.8) * mm, v(-299.02, 12.17) * mm, v(-298.36, 3.19) * mm, v(-306.93, -38.88) * mm]});
            skFitSpline(sketch, "E228", {"points": [v(-325.7, -74.88) * mm, v(-336.91, -74.88) * mm, v(-337.13, -74.73) * mm, v(-336.28, -67.25) * mm]});
            skFitSpline(sketch, "E229", {"points": [v(-336.28, -67.25) * mm, v(-335.8, -63.05) * mm, v(-333.24, -50.46) * mm, v(-330.57, -39.26) * mm]});
            skFitSpline(sketch, "E230", {"points": [v(-330.57, -39.26) * mm, v(-324.1, -12.02) * mm, v(-324.1, 4.23) * mm, v(-330.62, 7.71) * mm]});
            skFitSpline(sketch, "E231", {"points": [v(-330.62, 7.71) * mm, v(-337.68, 11.5) * mm, v(-344.92, 10.96) * mm, v(-348.72, 6.37) * mm]});
            skFitSpline(sketch, "E232", {"points": [v(-348.72, 6.37) * mm, v(-350.54, 4.19) * mm, v(-355.59, -14.99) * mm, v(-359.95, -36.24) * mm]});
            skLineSegment(sketch, "E233", {"start": v(-306.93, -38.88) * mm, "end": v(-314.26, -74.88) * mm});
            skLineSegment(sketch, "E234", {"start": v(-314.26, -74.88) * mm, "end": v(-325.7, -74.88) * mm});
            skFitSpline(sketch, "E235", {"points": [v(-378.35, -75.65) * mm, v(-384.12, -76.08) * mm, v(-389.34, -75.5) * mm, v(-389.96, -74.38) * mm]});
            skLineSegment(sketch, "E236", {"start": v(-359.95, -36.24) * mm, "end": v(-367.88, -74.88) * mm});
            skLineSegment(sketch, "E237", {"start": v(-367.88, -74.88) * mm, "end": v(-378.35, -75.65) * mm});
            skSolve(sketch);
        }
        {
            var Q0;
            Q0 = qSketchRegion(id + "F0", true);
            extrude(context, id + "F1", {"entities" : qUnion([Q0]), "depth" : 50 * mm, "offsetDistance" : 25 * mm});
        }
    });
